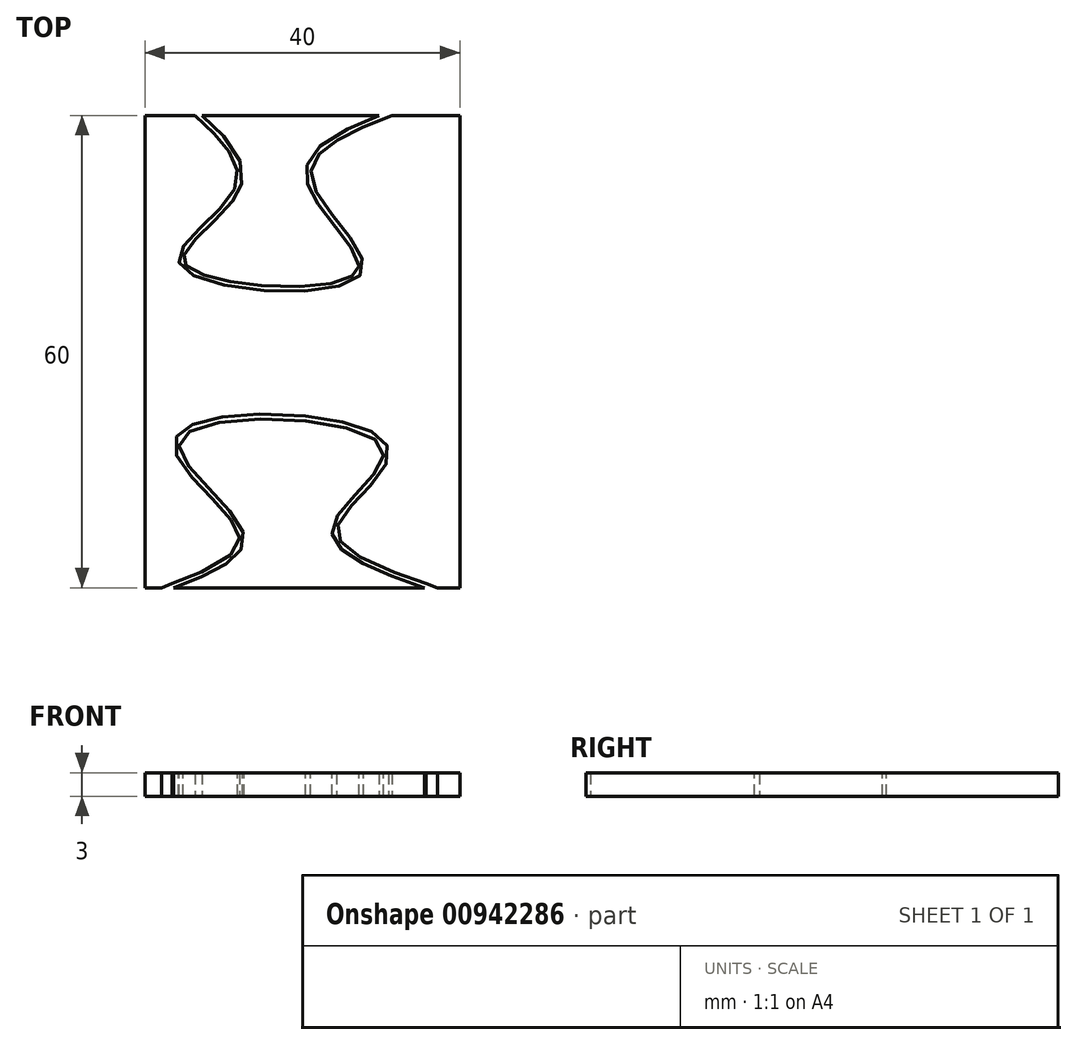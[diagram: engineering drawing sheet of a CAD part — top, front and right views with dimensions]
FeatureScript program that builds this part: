
annotation { "Feature Type Name" : "Feature", "Feature Type Description" : "" }
export const myFeature = defineFeature(function(context is Context, id is Id, definition is map)
    precondition{}
    {
        {
            var Q0;
            Q0=qCreatedBy(makeId("Top.planeOp"),FACE);
            var sketch = newSketch(context, id + "F0", { "sketchPlane" : qUnion([Q0])});
            skLineSegment(sketch, "E0.bottom", {"start": v(0, 0) * mm, "end": v(40, 0) * mm});
            skLineSegment(sketch, "E0.top", {"start": v(0, 60) * mm, "end": v(40, 60) * mm});
            skLineSegment(sketch, "E0.left", {"start": v(0, 0) * mm, "end": v(0, 60) * mm});
            skLineSegment(sketch, "E0.right", {"start": v(40, 0) * mm, "end": v(40, 60) * mm});
            skFitSpline(sketch, "E1", {"points": [v(3.64, 0) * mm, v(12.46, 7.04) * mm, v(4.59, 18.95) * mm, v(30.1, 17.99) * mm, v(23.85, 7.86) * mm, v(35.52, 0) * mm], "startDerivative": vector(84.8, 32.71) * mm, "endDerivative": vector(97.8, -34.18) * mm});
            skFitSpline(sketch, "E2", {"points": [v(6.4, 60) * mm, v(11.4, 50.76) * mm, v(4.48, 40.95) * mm, v(27.42, 39.8) * mm, v(21.13, 51.88) * mm, v(31.36, 60) * mm], "startDerivative": vector(56.24, -52.06) * mm, "endDerivative": vector(86.1, 33.94) * mm});
            skFitSpline(sketch, "E3.0", {"points": [v(3.43, 0.56) * mm, v(4.31, 0.9) * mm, v(6.07, 1.58) * mm, v(8.48, 2.63) * mm, v(10.1, 3.57) * mm, v(11.06, 4.36) * mm, v(11.58, 4.95) * mm, v(11.9, 5.54) * mm, v(12.01, 6.13) * mm, v(11.95, 6.67) * mm, v(11.78, 7.17) * mm, v(11.52, 7.72) * mm, v(11.03, 8.47) * mm, v(10.26, 9.44) * mm, v(9.34, 10.46) * mm, v(8.35, 11.5) * mm, v(7.33, 12.55) * mm, v(6.33, 13.6) * mm, v(5.42, 14.64) * mm, v(4.65, 15.66) * mm, v(4.06, 16.66) * mm, v(3.77, 17.5) * mm, v(3.73, 18.2) * mm, v(3.81, 18.73) * mm, v(4.03, 19.22) * mm, v(4.36, 19.66) * mm, v(4.78, 20.04) * mm, v(5.45, 20.47) * mm, v(6.45, 20.92) * mm, v(7.91, 21.33) * mm, v(9.59, 21.65) * mm, v(11.43, 21.87) * mm, v(14.08, 22.04) * mm, v(17.6, 22.04) * mm, v(21.1, 21.75) * mm, v(23.7, 21.36) * mm, v(25.52, 20.98) * mm, v(27.14, 20.52) * mm, v(28.55, 19.97) * mm, v(29.5, 19.44) * mm, v(30.1, 18.94) * mm, v(30.49, 18.52) * mm, v(30.77, 18.03) * mm, v(30.92, 17.52) * mm, v(30.95, 17) * mm, v(30.85, 16.31) * mm, v(30.52, 15.49) * mm, v(29.91, 14.53) * mm, v(29.14, 13.57) * mm, v(28.28, 12.61) * mm, v(27.37, 11.66) * mm, v(26.48, 10.71) * mm, v(25.67, 9.8) * mm, v(25, 8.92) * mm, v(24.62, 8.25) * mm, v(24.44, 7.78) * mm, v(24.34, 7.35) * mm, v(24.35, 6.86) * mm, v(24.55, 6.28) * mm, v(24.97, 5.68) * mm, v(25.6, 5.07) * mm, v(26.43, 4.46) * mm, v(27.77, 3.67) * mm, v(29.82, 2.72) * mm, v(32.67, 1.63) * mm, v(34.7, 0.92) * mm, v(35.72, 0.57) * mm]});
            skFitSpline(sketch, "E4.0", {"points": [v(6.8, 60.44) * mm, v(7.39, 59.9) * mm, v(8.57, 58.8) * mm, v(10.2, 57.14) * mm, v(11.5, 55.4) * mm, v(12.2, 53.87) * mm, v(12.4, 52.56) * mm, v(12.32, 51.56) * mm, v(12.06, 50.72) * mm, v(11.73, 50.05) * mm, v(11.33, 49.4) * mm, v(10.73, 48.61) * mm, v(9.6, 47.38) * mm, v(8.34, 46.17) * mm, v(7.13, 45.02) * mm, v(6.3, 44.18) * mm, v(5.62, 43.4) * mm, v(5.13, 42.67) * mm, v(4.9, 42.15) * mm, v(4.86, 41.81) * mm, v(4.87, 41.6) * mm, v(4.92, 41.4) * mm, v(5.03, 41.2) * mm, v(5.23, 40.96) * mm, v(5.62, 40.63) * mm, v(6.33, 40.21) * mm, v(7.48, 39.74) * mm, v(8.88, 39.32) * mm, v(10.46, 38.97) * mm, v(12.18, 38.68) * mm, v(14.6, 38.39) * mm, v(17.77, 38.21) * mm, v(20.78, 38.3) * mm, v(22.92, 38.56) * mm, v(24.34, 38.84) * mm, v(25.52, 39.2) * mm, v(26.27, 39.56) * mm, v(26.68, 39.87) * mm, v(26.9, 40.1) * mm, v(27.04, 40.3) * mm, v(27.15, 40.61) * mm, v(27.17, 41.07) * mm, v(26.96, 41.8) * mm, v(26.54, 42.66) * mm, v(25.93, 43.6) * mm, v(25.19, 44.61) * mm, v(24.1, 46) * mm, v(22.93, 47.45) * mm, v(21.9, 48.88) * mm, v(21.24, 49.95) * mm, v(20.81, 50.84) * mm, v(20.59, 51.55) * mm, v(20.44, 52.26) * mm, v(20.44, 53.12) * mm, v(20.71, 54.09) * mm, v(21.2, 54.96) * mm, v(22.11, 56.02) * mm, v(23.62, 57.17) * mm, v(25.88, 58.38) * mm, v(28.44, 59.5) * mm, v(30.24, 60.2) * mm, v(31.14, 60.56) * mm]});
            skLineSegment(sketch, "E5", {"start": v(3.43, 0.56) * mm, "end": v(1.09, -0.41) * mm});
            skLineSegment(sketch, "E6", {"start": v(35.72, 0.57) * mm, "end": v(38.11, -0.37) * mm});
            skSolve(sketch);
        }
        {
            var Q0;
            {var subQ0=sQuery(id+"F0.wireOp",EDGE,"E4.0");var subQ1=sQuery(id+"F0.wireOp",EDGE,"E0.top");var subQ2=makeQuery(id+"F0.imprint","INTERSECT",VERTEX,{"disambiguationData":[OD(0.0)],"derivedFrom":[subQ1,subQ0]});Q0=makeQuery(id+"F0.imprint","IMPRINT",FACE,{"disambiguationData":[TD([[makeQuery(id+"F0.imprint","IMPRINT",EDGE,{"disambiguationData":[TD([[subQ2,-1.0]])],"derivedFrom":subQ1}),-1.0]])]});}
            var Q1;
            {var subQ0=sQuery(id+"F0.wireOp",EDGE,"E0.left");Q1=makeQuery(id+"F0.imprint","IMPRINT",FACE,{"disambiguationData":[TD([[makeQuery(id+"F0.imprint","IMPRINT",EDGE,{"derivedFrom":subQ0}),-1.0]])]});}
            var Q2;
            {var subQ0=sQuery(id+"F0.wireOp",EDGE,"E1");Q2=makeQuery(id+"F0.imprint","IMPRINT",FACE,{"disambiguationData":[TD([[makeQuery(id+"F0.imprint","IMPRINT",EDGE,{"derivedFrom":subQ0}),-1.0]])]});}
            var Q3;
            {var subQ0=sQuery(id+"F0.wireOp",EDGE,"E2");Q3=makeQuery(id+"F0.imprint","IMPRINT",FACE,{"disambiguationData":[TD([[makeQuery(id+"F0.imprint","IMPRINT",EDGE,{"derivedFrom":subQ0}),1.0]])]});}
            extrude(context, id + "F1", {"entities" : qUnion([Q0, Q1, Q2, Q3]), "depth" : 3 * mm, "offsetDistance" : 25 * mm});
        }
        {
            var Q0;
            {var subQ0=sQuery(id+"F0.wireOp",EDGE,"E2");Q0=makeQuery(id+"F0.imprint","IMPRINT",FACE,{"disambiguationData":[TD([[makeQuery(id+"F0.imprint","IMPRINT",EDGE,{"derivedFrom":subQ0}),1.0]])]});}
            extrude(context, id + "F2", {"entities" : qUnion([Q0]), "operationType" : NewBodyOperationType.REMOVE, "oppositeDirection" : true, "depth" : -5 * mm, "offsetDistance" : 25 * mm});
        }
    });
